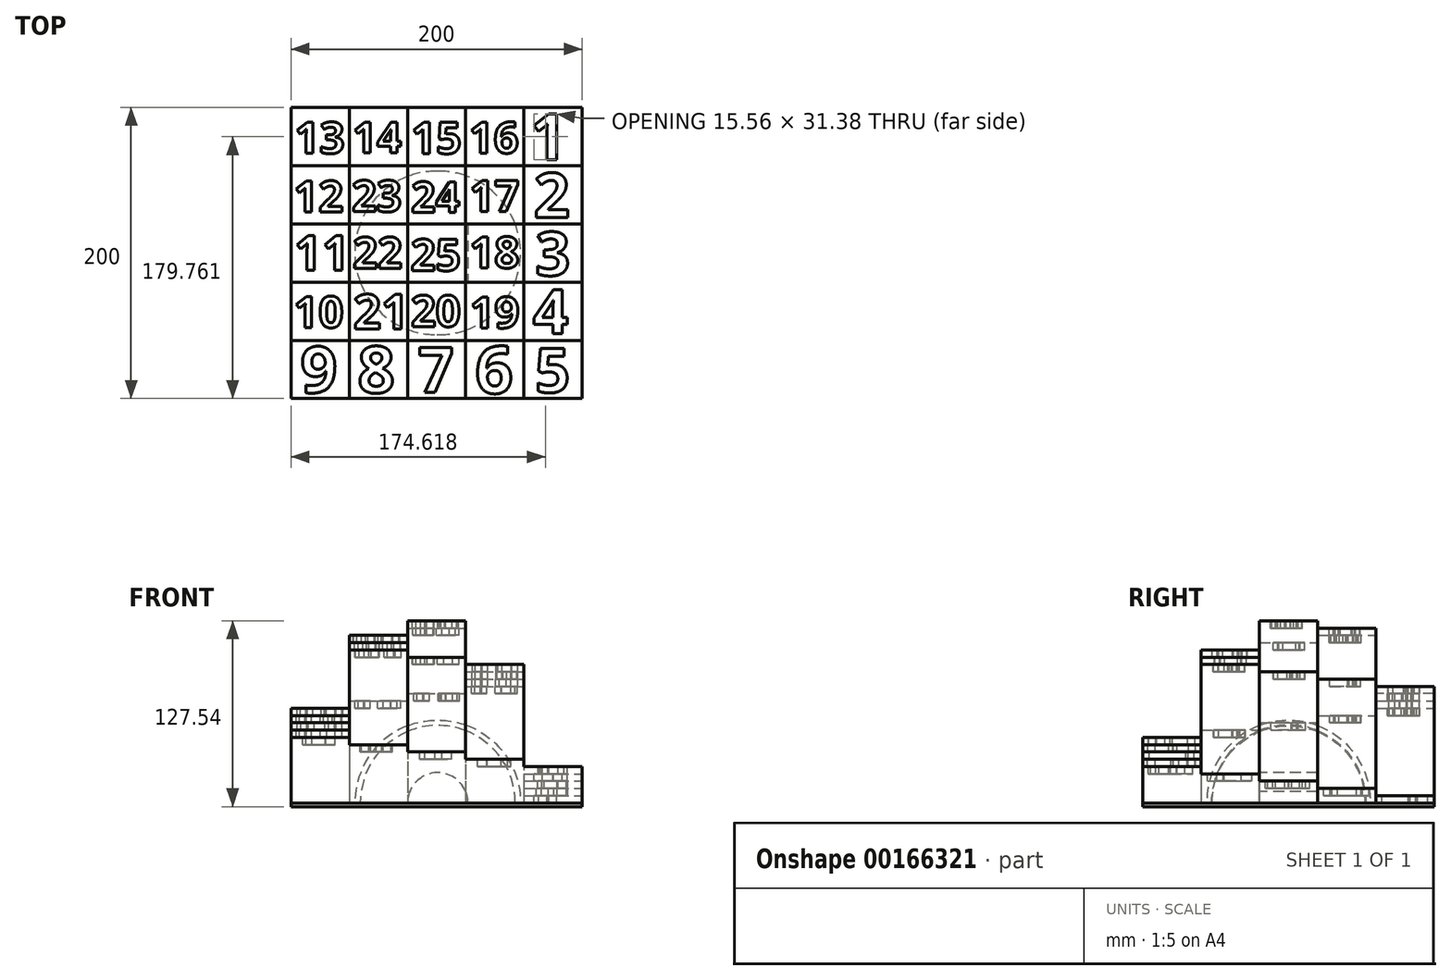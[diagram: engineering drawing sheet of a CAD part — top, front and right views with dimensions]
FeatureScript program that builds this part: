
annotation { "Feature Type Name" : "Feature", "Feature Type Description" : "" }
export const myFeature = defineFeature(function(context is Context, id is Id, definition is map)
    precondition{}
    {
        {
            var Q0;
            Q0=qCreatedBy(makeId("Top.planeOp"),FACE);
            var sketch = newSketch(context, id + "F0", { "sketchPlane" : qUnion([Q0])});
            skLineSegment(sketch, "E0.bottom", {"start": v(-166.14, 98.83) * mm, "end": v(33.86, 98.83) * mm});
            skLineSegment(sketch, "E0.top", {"start": v(-166.14, -101.17) * mm, "end": v(33.86, -101.17) * mm});
            skLineSegment(sketch, "E0.left", {"start": v(-166.14, 98.83) * mm, "end": v(-166.14, -101.17) * mm});
            skLineSegment(sketch, "E0.right", {"start": v(33.86, 98.83) * mm, "end": v(33.86, -101.17) * mm});
            skLineSegment(sketch, "E1", {"start": v(-166.14, 58.83) * mm, "end": v(33.86, 58.83) * mm});
            skLineSegment(sketch, "E2", {"start": v(-166.14, 18.83) * mm, "end": v(33.86, 18.83) * mm});
            skLineSegment(sketch, "E3", {"start": v(-166.14, -21.17) * mm, "end": v(33.86, -21.17) * mm});
            skLineSegment(sketch, "E4", {"start": v(-166.14, -61.17) * mm, "end": v(33.86, -61.17) * mm});
            skLineSegment(sketch, "E5", {"start": v(-126.14, 98.83) * mm, "end": v(-126.14, -101.17) * mm});
            skLineSegment(sketch, "E6", {"start": v(-86.14, 98.83) * mm, "end": v(-86.14, -101.17) * mm});
            skLineSegment(sketch, "E7", {"start": v(-46.14, 98.83) * mm, "end": v(-46.14, -101.17) * mm});
            skLineSegment(sketch, "E8", {"start": v(-6.14, 98.83) * mm, "end": v(-6.14, -101.17) * mm});
            skSolve(sketch);
        }
        {
            var Q0;
            {var subQ0=sQuery(id+"F0.wireOp",EDGE,"E0.left");var subQ1=sQuery(id+"F0.wireOp",EDGE,"E0.bottom");var subQ2=makeQuery(id+"F0.imprint","INTERSECT",VERTEX,{"derivedFrom":[subQ1,subQ0]});Q0=makeQuery(id+"F0.imprint","IMPRINT",FACE,{"disambiguationData":[TD([[makeQuery(id+"F0.imprint","IMPRINT",EDGE,{"disambiguationData":[TD([[subQ2,-1.0]])],"derivedFrom":subQ1}),-1.0]])]});}
            extrude(context, id + "F1", {"entities" : qUnion([Q0]), "depth" : 5 * mm});
        }
        {
            var Q0;
            Q0=makeQuery(id+"F1.opExtrude","CAP_FACE",FACE,{"disambiguationData":[OSD([sQuery(id+"F0.wireOp",EDGE,"E0.bottom"),sQuery(id+"F0.wireOp",EDGE,"E0.left"),sQuery(id+"F0.wireOp",EDGE,"E1"),sQuery(id+"F0.wireOp",EDGE,"E5")])],"isStart":true});
            var sketch = newSketch(context, id + "F2", { "sketchPlane" : qUnion([Q0])});
            skLineSegment(sketch, "E9.bottom", {"start": v(-166.14, -58.83) * mm, "end": v(-126.14, -58.83) * mm});
            skLineSegment(sketch, "E9.top", {"start": v(-166.14, -18.83) * mm, "end": v(-126.14, -18.83) * mm});
            skLineSegment(sketch, "E9.left", {"start": v(-166.14, -58.83) * mm, "end": v(-166.14, -18.83) * mm});
            skLineSegment(sketch, "E9.right", {"start": v(-126.14, -58.83) * mm, "end": v(-126.14, -18.83) * mm});
            skSolve(sketch);
        }
        {
            var Q0;
            Q0 = qSketchRegion(id + "F2", true);
            extrude(context, id + "F3", {"entities" : qUnion([Q0]), "oppositeDirection" : true, "depth" : 10 * mm});
        }
        {
            var Q0;
            Q0=makeQuery(id+"F3.opExtrude","CAP_FACE",FACE,{"disambiguationData":[OSD([sQuery(id+"F2.wireOp",EDGE,"E9.bottom"),sQuery(id+"F2.wireOp",EDGE,"E9.top"),sQuery(id+"F2.wireOp",EDGE,"E9.left"),sQuery(id+"F2.wireOp",EDGE,"E9.right")])],"isStart":true});
            var sketch = newSketch(context, id + "F4", { "sketchPlane" : qUnion([Q0])});
            skLineSegment(sketch, "E10.bottom", {"start": v(-166.14, -18.83) * mm, "end": v(-126.14, -18.83) * mm});
            skLineSegment(sketch, "E10.top", {"start": v(-166.14, 21.17) * mm, "end": v(-126.14, 21.17) * mm});
            skLineSegment(sketch, "E10.left", {"start": v(-166.14, -18.83) * mm, "end": v(-166.14, 21.17) * mm});
            skLineSegment(sketch, "E10.right", {"start": v(-126.14, -18.83) * mm, "end": v(-126.14, 21.17) * mm});
            skSolve(sketch);
        }
        {
            var Q0;
            Q0 = qSketchRegion(id + "F4", true);
            extrude(context, id + "F5", {"entities" : qUnion([Q0]), "oppositeDirection" : true, "depth" : 15 * mm});
        }
        {
            var Q0;
            Q0=makeQuery(id+"F5.opExtrude","CAP_FACE",FACE,{"disambiguationData":[OSD([sQuery(id+"F4.wireOp",EDGE,"E10.bottom"),sQuery(id+"F4.wireOp",EDGE,"E10.top"),sQuery(id+"F4.wireOp",EDGE,"E10.left"),sQuery(id+"F4.wireOp",EDGE,"E10.right")])],"isStart":true});
            var sketch = newSketch(context, id + "F6", { "sketchPlane" : qUnion([Q0])});
            skLineSegment(sketch, "E11.bottom", {"start": v(-166.14, 21.17) * mm, "end": v(-126.14, 21.17) * mm});
            skLineSegment(sketch, "E11.top", {"start": v(-166.14, 61.17) * mm, "end": v(-126.14, 61.17) * mm});
            skLineSegment(sketch, "E11.left", {"start": v(-166.14, 21.17) * mm, "end": v(-166.14, 61.17) * mm});
            skLineSegment(sketch, "E11.right", {"start": v(-126.14, 21.17) * mm, "end": v(-126.14, 61.17) * mm});
            skSolve(sketch);
        }
        {
            var Q0;
            Q0 = qSketchRegion(id + "F6", true);
            extrude(context, id + "F7", {"entities" : qUnion([Q0]), "operationType" : NewBodyOperationType.ADD, "oppositeDirection" : true, "depth" : 20 * mm});
        }
        {
            var Q0;
            Q0=makeQuery(id+"F7.boolean.opBoolean","MERGE",FACE,{"derivedFrom":[makeQuery(id+"F5.opExtrude","CAP_FACE",FACE,{"disambiguationData":[OSD([sQuery(id+"F4.wireOp",EDGE,"E10.bottom"),sQuery(id+"F4.wireOp",EDGE,"E10.top"),sQuery(id+"F4.wireOp",EDGE,"E10.left"),sQuery(id+"F4.wireOp",EDGE,"E10.right")])],"isStart":true}),makeQuery(id+"F7.opExtrude","CAP_FACE",FACE,{"disambiguationData":[OSD([sQuery(id+"F6.wireOp",EDGE,"E11.bottom"),sQuery(id+"F6.wireOp",EDGE,"E11.top"),sQuery(id+"F6.wireOp",EDGE,"E11.left"),sQuery(id+"F6.wireOp",EDGE,"E11.right")])],"isStart":true})]});
            var sketch = newSketch(context, id + "F8", { "sketchPlane" : qUnion([Q0])});
            skLineSegment(sketch, "E12.bottom", {"start": v(-166.14, 61.17) * mm, "end": v(-126.14, 61.17) * mm});
            skLineSegment(sketch, "E12.top", {"start": v(-166.14, 101.17) * mm, "end": v(-126.14, 101.17) * mm});
            skLineSegment(sketch, "E12.left", {"start": v(-166.14, 61.17) * mm, "end": v(-166.14, 101.17) * mm});
            skLineSegment(sketch, "E12.right", {"start": v(-126.14, 61.17) * mm, "end": v(-126.14, 101.17) * mm});
            skSolve(sketch);
        }
        {
            var Q0;
            Q0 = qSketchRegion(id + "F8", true);
            extrude(context, id + "F9", {"entities" : qUnion([Q0]), "oppositeDirection" : true, "depth" : 25 * mm});
        }
        {
            var Q0;
            Q0=makeQuery(id+"F9.opExtrude","CAP_FACE",FACE,{"disambiguationData":[OSD([sQuery(id+"F8.wireOp",EDGE,"E12.bottom"),sQuery(id+"F8.wireOp",EDGE,"E12.top"),sQuery(id+"F8.wireOp",EDGE,"E12.left"),sQuery(id+"F8.wireOp",EDGE,"E12.right")])],"isStart":true});
            var sketch = newSketch(context, id + "F10", { "sketchPlane" : qUnion([Q0])});
            skLineSegment(sketch, "E13.bottom", {"start": v(-166.14, 61.17) * mm, "end": v(-206.14, 61.17) * mm});
            skLineSegment(sketch, "E13.top", {"start": v(-166.14, 101.17) * mm, "end": v(-206.14, 101.17) * mm});
            skLineSegment(sketch, "E13.left", {"start": v(-166.14, 61.17) * mm, "end": v(-166.14, 101.17) * mm});
            skLineSegment(sketch, "E13.right", {"start": v(-206.14, 61.17) * mm, "end": v(-206.14, 101.17) * mm});
            skSolve(sketch);
        }
        {
            var Q0;
            Q0 = qSketchRegion(id + "F10", true);
            extrude(context, id + "F11", {"entities" : qUnion([Q0]), "operationType" : NewBodyOperationType.ADD, "oppositeDirection" : true, "depth" : 30 * mm});
        }
        {
            var Q0;
            Q0=makeQuery(id+"F11.boolean.opBoolean","MERGE",FACE,{"derivedFrom":[makeQuery(id+"F9.opExtrude","CAP_FACE",FACE,{"disambiguationData":[OSD([sQuery(id+"F8.wireOp",EDGE,"E12.bottom"),sQuery(id+"F8.wireOp",EDGE,"E12.top"),sQuery(id+"F8.wireOp",EDGE,"E12.left"),sQuery(id+"F8.wireOp",EDGE,"E12.right")])],"isStart":true}),makeQuery(id+"F11.opExtrude","CAP_FACE",FACE,{"disambiguationData":[OSD([sQuery(id+"F10.wireOp",EDGE,"E13.bottom"),sQuery(id+"F10.wireOp",EDGE,"E13.top"),sQuery(id+"F10.wireOp",EDGE,"E13.left"),sQuery(id+"F10.wireOp",EDGE,"E13.right")])],"isStart":true})]});
            var sketch = newSketch(context, id + "F12", { "sketchPlane" : qUnion([Q0])});
            skLineSegment(sketch, "E14.bottom", {"start": v(-206.14, 61.17) * mm, "end": v(-246.14, 61.17) * mm});
            skLineSegment(sketch, "E14.top", {"start": v(-206.14, 101.17) * mm, "end": v(-246.14, 101.17) * mm});
            skLineSegment(sketch, "E14.left", {"start": v(-206.14, 61.17) * mm, "end": v(-206.14, 101.17) * mm});
            skLineSegment(sketch, "E14.right", {"start": v(-246.14, 61.17) * mm, "end": v(-246.14, 101.17) * mm});
            skSolve(sketch);
        }
        {
            var Q0;
            Q0 = qSketchRegion(id + "F12", true);
            extrude(context, id + "F13", {"entities" : qUnion([Q0]), "operationType" : NewBodyOperationType.ADD, "oppositeDirection" : true, "depth" : 35 * mm});
        }
        {
            var Q0;
            Q0=makeQuery(id+"F13.boolean.opBoolean","MERGE",FACE,{"derivedFrom":[makeQuery(id+"F11.boolean.opBoolean","MERGE",FACE,{"derivedFrom":[makeQuery(id+"F9.opExtrude","CAP_FACE",FACE,{"disambiguationData":[OSD([sQuery(id+"F8.wireOp",EDGE,"E12.bottom"),sQuery(id+"F8.wireOp",EDGE,"E12.top"),sQuery(id+"F8.wireOp",EDGE,"E12.left"),sQuery(id+"F8.wireOp",EDGE,"E12.right")])],"isStart":true}),makeQuery(id+"F11.opExtrude","CAP_FACE",FACE,{"disambiguationData":[OSD([sQuery(id+"F10.wireOp",EDGE,"E13.bottom"),sQuery(id+"F10.wireOp",EDGE,"E13.top"),sQuery(id+"F10.wireOp",EDGE,"E13.left"),sQuery(id+"F10.wireOp",EDGE,"E13.right")])],"isStart":true})]}),makeQuery(id+"F13.opExtrude","CAP_FACE",FACE,{"disambiguationData":[OSD([sQuery(id+"F12.wireOp",EDGE,"E14.bottom"),sQuery(id+"F12.wireOp",EDGE,"E14.top"),sQuery(id+"F12.wireOp",EDGE,"E14.left"),sQuery(id+"F12.wireOp",EDGE,"E14.right")])],"isStart":true})]});
            var sketch = newSketch(context, id + "F14", { "sketchPlane" : qUnion([Q0])});
            skLineSegment(sketch, "E15.bottom", {"start": v(-246.14, 61.17) * mm, "end": v(-286.14, 61.17) * mm});
            skLineSegment(sketch, "E15.top", {"start": v(-246.14, 101.17) * mm, "end": v(-286.14, 101.17) * mm});
            skLineSegment(sketch, "E15.left", {"start": v(-246.14, 61.17) * mm, "end": v(-246.14, 101.17) * mm});
            skLineSegment(sketch, "E15.right", {"start": v(-286.14, 61.17) * mm, "end": v(-286.14, 101.17) * mm});
            skSolve(sketch);
        }
        {
            var Q0;
            Q0 = qSketchRegion(id + "F14", true);
            extrude(context, id + "F15", {"entities" : qUnion([Q0]), "operationType" : NewBodyOperationType.ADD, "oppositeDirection" : true, "depth" : 40 * mm});
        }
        {
            var Q0;
            Q0=makeQuery(id+"F15.boolean.opBoolean","MERGE",FACE,{"derivedFrom":[makeQuery(id+"F13.boolean.opBoolean","MERGE",FACE,{"derivedFrom":[makeQuery(id+"F11.boolean.opBoolean","MERGE",FACE,{"derivedFrom":[makeQuery(id+"F9.opExtrude","CAP_FACE",FACE,{"disambiguationData":[OSD([sQuery(id+"F8.wireOp",EDGE,"E12.bottom"),sQuery(id+"F8.wireOp",EDGE,"E12.top"),sQuery(id+"F8.wireOp",EDGE,"E12.left"),sQuery(id+"F8.wireOp",EDGE,"E12.right")])],"isStart":true}),makeQuery(id+"F11.opExtrude","CAP_FACE",FACE,{"disambiguationData":[OSD([sQuery(id+"F10.wireOp",EDGE,"E13.bottom"),sQuery(id+"F10.wireOp",EDGE,"E13.top"),sQuery(id+"F10.wireOp",EDGE,"E13.left"),sQuery(id+"F10.wireOp",EDGE,"E13.right")])],"isStart":true})]}),makeQuery(id+"F13.opExtrude","CAP_FACE",FACE,{"disambiguationData":[OSD([sQuery(id+"F12.wireOp",EDGE,"E14.bottom"),sQuery(id+"F12.wireOp",EDGE,"E14.top"),sQuery(id+"F12.wireOp",EDGE,"E14.left"),sQuery(id+"F12.wireOp",EDGE,"E14.right")])],"isStart":true})]}),makeQuery(id+"F15.opExtrude","CAP_FACE",FACE,{"disambiguationData":[OSD([sQuery(id+"F14.wireOp",EDGE,"E15.bottom"),sQuery(id+"F14.wireOp",EDGE,"E15.top"),sQuery(id+"F14.wireOp",EDGE,"E15.left"),sQuery(id+"F14.wireOp",EDGE,"E15.right")])],"isStart":true})]});
            var sketch = newSketch(context, id + "F16", { "sketchPlane" : qUnion([Q0])});
            skLineSegment(sketch, "E16.bottom", {"start": v(-286.14, 61.17) * mm, "end": v(-326.14, 61.17) * mm});
            skLineSegment(sketch, "E16.top", {"start": v(-286.14, 101.17) * mm, "end": v(-326.14, 101.17) * mm});
            skLineSegment(sketch, "E16.left", {"start": v(-286.14, 61.17) * mm, "end": v(-286.14, 101.17) * mm});
            skLineSegment(sketch, "E16.right", {"start": v(-326.14, 61.17) * mm, "end": v(-326.14, 101.17) * mm});
            skSolve(sketch);
        }
        {
            var Q0;
            Q0 = qSketchRegion(id + "F16", true);
            extrude(context, id + "F17", {"entities" : qUnion([Q0]), "operationType" : NewBodyOperationType.ADD, "oppositeDirection" : true, "depth" : 45 * mm});
        }
        {
            var Q0;
            Q0=makeQuery(id+"F17.boolean.opBoolean","MERGE",FACE,{"derivedFrom":[makeQuery(id+"F15.boolean.opBoolean","MERGE",FACE,{"derivedFrom":[makeQuery(id+"F13.boolean.opBoolean","MERGE",FACE,{"derivedFrom":[makeQuery(id+"F11.boolean.opBoolean","MERGE",FACE,{"derivedFrom":[makeQuery(id+"F9.opExtrude","CAP_FACE",FACE,{"disambiguationData":[OSD([sQuery(id+"F8.wireOp",EDGE,"E12.bottom"),sQuery(id+"F8.wireOp",EDGE,"E12.top"),sQuery(id+"F8.wireOp",EDGE,"E12.left"),sQuery(id+"F8.wireOp",EDGE,"E12.right")])],"isStart":true}),makeQuery(id+"F11.opExtrude","CAP_FACE",FACE,{"disambiguationData":[OSD([sQuery(id+"F10.wireOp",EDGE,"E13.bottom"),sQuery(id+"F10.wireOp",EDGE,"E13.top"),sQuery(id+"F10.wireOp",EDGE,"E13.left"),sQuery(id+"F10.wireOp",EDGE,"E13.right")])],"isStart":true})]}),makeQuery(id+"F13.opExtrude","CAP_FACE",FACE,{"disambiguationData":[OSD([sQuery(id+"F12.wireOp",EDGE,"E14.bottom"),sQuery(id+"F12.wireOp",EDGE,"E14.top"),sQuery(id+"F12.wireOp",EDGE,"E14.left"),sQuery(id+"F12.wireOp",EDGE,"E14.right")])],"isStart":true})]}),makeQuery(id+"F15.opExtrude","CAP_FACE",FACE,{"disambiguationData":[OSD([sQuery(id+"F14.wireOp",EDGE,"E15.bottom"),sQuery(id+"F14.wireOp",EDGE,"E15.top"),sQuery(id+"F14.wireOp",EDGE,"E15.left"),sQuery(id+"F14.wireOp",EDGE,"E15.right")])],"isStart":true})]}),makeQuery(id+"F17.opExtrude","CAP_FACE",FACE,{"disambiguationData":[OSD([sQuery(id+"F16.wireOp",EDGE,"E16.bottom"),sQuery(id+"F16.wireOp",EDGE,"E16.top"),sQuery(id+"F16.wireOp",EDGE,"E16.left"),sQuery(id+"F16.wireOp",EDGE,"E16.right")])],"isStart":true})]});
            var sketch = newSketch(context, id + "F18", { "sketchPlane" : qUnion([Q0])});
            skLineSegment(sketch, "E17.bottom", {"start": v(-326.14, 61.17) * mm, "end": v(-286.14, 61.17) * mm});
            skLineSegment(sketch, "E17.top", {"start": v(-326.14, 21.17) * mm, "end": v(-286.14, 21.17) * mm});
            skLineSegment(sketch, "E17.left", {"start": v(-326.14, 61.17) * mm, "end": v(-326.14, 21.17) * mm});
            skLineSegment(sketch, "E17.right", {"start": v(-286.14, 61.17) * mm, "end": v(-286.14, 21.17) * mm});
            skSolve(sketch);
        }
        {
            var Q0;
            Q0 = qSketchRegion(id + "F18", true);
            extrude(context, id + "F19", {"entities" : qUnion([Q0]), "operationType" : NewBodyOperationType.ADD, "oppositeDirection" : true, "depth" : 50 * mm});
        }
        {
            var Q0;
            Q0=makeQuery(id+"F19.boolean.opBoolean","MERGE",FACE,{"derivedFrom":[makeQuery(id+"F17.boolean.opBoolean","MERGE",FACE,{"derivedFrom":[makeQuery(id+"F15.boolean.opBoolean","MERGE",FACE,{"derivedFrom":[makeQuery(id+"F13.boolean.opBoolean","MERGE",FACE,{"derivedFrom":[makeQuery(id+"F11.boolean.opBoolean","MERGE",FACE,{"derivedFrom":[makeQuery(id+"F9.opExtrude","CAP_FACE",FACE,{"disambiguationData":[OSD([sQuery(id+"F8.wireOp",EDGE,"E12.bottom"),sQuery(id+"F8.wireOp",EDGE,"E12.top"),sQuery(id+"F8.wireOp",EDGE,"E12.left"),sQuery(id+"F8.wireOp",EDGE,"E12.right")])],"isStart":true}),makeQuery(id+"F11.opExtrude","CAP_FACE",FACE,{"disambiguationData":[OSD([sQuery(id+"F10.wireOp",EDGE,"E13.bottom"),sQuery(id+"F10.wireOp",EDGE,"E13.top"),sQuery(id+"F10.wireOp",EDGE,"E13.left"),sQuery(id+"F10.wireOp",EDGE,"E13.right")])],"isStart":true})]}),makeQuery(id+"F13.opExtrude","CAP_FACE",FACE,{"disambiguationData":[OSD([sQuery(id+"F12.wireOp",EDGE,"E14.bottom"),sQuery(id+"F12.wireOp",EDGE,"E14.top"),sQuery(id+"F12.wireOp",EDGE,"E14.left"),sQuery(id+"F12.wireOp",EDGE,"E14.right")])],"isStart":true})]}),makeQuery(id+"F15.opExtrude","CAP_FACE",FACE,{"disambiguationData":[OSD([sQuery(id+"F14.wireOp",EDGE,"E15.bottom"),sQuery(id+"F14.wireOp",EDGE,"E15.top"),sQuery(id+"F14.wireOp",EDGE,"E15.left"),sQuery(id+"F14.wireOp",EDGE,"E15.right")])],"isStart":true})]}),makeQuery(id+"F17.opExtrude","CAP_FACE",FACE,{"disambiguationData":[OSD([sQuery(id+"F16.wireOp",EDGE,"E16.bottom"),sQuery(id+"F16.wireOp",EDGE,"E16.top"),sQuery(id+"F16.wireOp",EDGE,"E16.left"),sQuery(id+"F16.wireOp",EDGE,"E16.right")])],"isStart":true})]}),makeQuery(id+"F19.opExtrude","CAP_FACE",FACE,{"disambiguationData":[OSD([sQuery(id+"F18.wireOp",EDGE,"E17.bottom"),sQuery(id+"F18.wireOp",EDGE,"E17.top"),sQuery(id+"F18.wireOp",EDGE,"E17.left"),sQuery(id+"F18.wireOp",EDGE,"E17.right")])],"isStart":true})]});
            var sketch = newSketch(context, id + "F20", { "sketchPlane" : qUnion([Q0])});
            skLineSegment(sketch, "E18.bottom", {"start": v(-326.14, 21.17) * mm, "end": v(-286.14, 21.17) * mm});
            skLineSegment(sketch, "E18.top", {"start": v(-326.14, -18.83) * mm, "end": v(-286.14, -18.83) * mm});
            skLineSegment(sketch, "E18.left", {"start": v(-326.14, 21.17) * mm, "end": v(-326.14, -18.83) * mm});
            skLineSegment(sketch, "E18.right", {"start": v(-286.14, 21.17) * mm, "end": v(-286.14, -18.83) * mm});
            skSolve(sketch);
        }
        {
            var Q0;
            Q0 = qSketchRegion(id + "F20", true);
            extrude(context, id + "F21", {"entities" : qUnion([Q0]), "operationType" : NewBodyOperationType.ADD, "oppositeDirection" : true, "depth" : 55 * mm});
        }
        {
            var Q0;
            Q0=makeQuery(id+"F21.boolean.opBoolean","MERGE",FACE,{"derivedFrom":[makeQuery(id+"F19.boolean.opBoolean","MERGE",FACE,{"derivedFrom":[makeQuery(id+"F17.boolean.opBoolean","MERGE",FACE,{"derivedFrom":[makeQuery(id+"F15.boolean.opBoolean","MERGE",FACE,{"derivedFrom":[makeQuery(id+"F13.boolean.opBoolean","MERGE",FACE,{"derivedFrom":[makeQuery(id+"F11.boolean.opBoolean","MERGE",FACE,{"derivedFrom":[makeQuery(id+"F9.opExtrude","CAP_FACE",FACE,{"disambiguationData":[OSD([sQuery(id+"F8.wireOp",EDGE,"E12.bottom"),sQuery(id+"F8.wireOp",EDGE,"E12.top"),sQuery(id+"F8.wireOp",EDGE,"E12.left"),sQuery(id+"F8.wireOp",EDGE,"E12.right")])],"isStart":true}),makeQuery(id+"F11.opExtrude","CAP_FACE",FACE,{"disambiguationData":[OSD([sQuery(id+"F10.wireOp",EDGE,"E13.bottom"),sQuery(id+"F10.wireOp",EDGE,"E13.top"),sQuery(id+"F10.wireOp",EDGE,"E13.left"),sQuery(id+"F10.wireOp",EDGE,"E13.right")])],"isStart":true})]}),makeQuery(id+"F13.opExtrude","CAP_FACE",FACE,{"disambiguationData":[OSD([sQuery(id+"F12.wireOp",EDGE,"E14.bottom"),sQuery(id+"F12.wireOp",EDGE,"E14.top"),sQuery(id+"F12.wireOp",EDGE,"E14.left"),sQuery(id+"F12.wireOp",EDGE,"E14.right")])],"isStart":true})]}),makeQuery(id+"F15.opExtrude","CAP_FACE",FACE,{"disambiguationData":[OSD([sQuery(id+"F14.wireOp",EDGE,"E15.bottom"),sQuery(id+"F14.wireOp",EDGE,"E15.top"),sQuery(id+"F14.wireOp",EDGE,"E15.left"),sQuery(id+"F14.wireOp",EDGE,"E15.right")])],"isStart":true})]}),makeQuery(id+"F17.opExtrude","CAP_FACE",FACE,{"disambiguationData":[OSD([sQuery(id+"F16.wireOp",EDGE,"E16.bottom"),sQuery(id+"F16.wireOp",EDGE,"E16.top"),sQuery(id+"F16.wireOp",EDGE,"E16.left"),sQuery(id+"F16.wireOp",EDGE,"E16.right")])],"isStart":true})]}),makeQuery(id+"F19.opExtrude","CAP_FACE",FACE,{"disambiguationData":[OSD([sQuery(id+"F18.wireOp",EDGE,"E17.bottom"),sQuery(id+"F18.wireOp",EDGE,"E17.top"),sQuery(id+"F18.wireOp",EDGE,"E17.left"),sQuery(id+"F18.wireOp",EDGE,"E17.right")])],"isStart":true})]}),makeQuery(id+"F21.opExtrude","CAP_FACE",FACE,{"disambiguationData":[OSD([sQuery(id+"F20.wireOp",EDGE,"E18.bottom"),sQuery(id+"F20.wireOp",EDGE,"E18.top"),sQuery(id+"F20.wireOp",EDGE,"E18.left"),sQuery(id+"F20.wireOp",EDGE,"E18.right")])],"isStart":true})]});
            var sketch = newSketch(context, id + "F22", { "sketchPlane" : qUnion([Q0])});
            skLineSegment(sketch, "E19.bottom", {"start": v(-326.14, -18.83) * mm, "end": v(-286.14, -18.83) * mm});
            skLineSegment(sketch, "E19.top", {"start": v(-326.14, -58.83) * mm, "end": v(-286.14, -58.83) * mm});
            skLineSegment(sketch, "E19.left", {"start": v(-326.14, -18.83) * mm, "end": v(-326.14, -58.83) * mm});
            skLineSegment(sketch, "E19.right", {"start": v(-286.14, -18.83) * mm, "end": v(-286.14, -58.83) * mm});
            skSolve(sketch);
        }
        {
            var Q0;
            Q0 = qSketchRegion(id + "F22", true);
            extrude(context, id + "F23", {"entities" : qUnion([Q0]), "operationType" : NewBodyOperationType.ADD, "oppositeDirection" : true, "depth" : 60 * mm});
        }
        {
            var Q0;
            Q0=makeQuery(id+"F23.boolean.opBoolean","MERGE",FACE,{"derivedFrom":[makeQuery(id+"F21.boolean.opBoolean","MERGE",FACE,{"derivedFrom":[makeQuery(id+"F19.boolean.opBoolean","MERGE",FACE,{"derivedFrom":[makeQuery(id+"F17.boolean.opBoolean","MERGE",FACE,{"derivedFrom":[makeQuery(id+"F15.boolean.opBoolean","MERGE",FACE,{"derivedFrom":[makeQuery(id+"F13.boolean.opBoolean","MERGE",FACE,{"derivedFrom":[makeQuery(id+"F11.boolean.opBoolean","MERGE",FACE,{"derivedFrom":[makeQuery(id+"F9.opExtrude","CAP_FACE",FACE,{"disambiguationData":[OSD([sQuery(id+"F8.wireOp",EDGE,"E12.bottom"),sQuery(id+"F8.wireOp",EDGE,"E12.top"),sQuery(id+"F8.wireOp",EDGE,"E12.left"),sQuery(id+"F8.wireOp",EDGE,"E12.right")])],"isStart":true}),makeQuery(id+"F11.opExtrude","CAP_FACE",FACE,{"disambiguationData":[OSD([sQuery(id+"F10.wireOp",EDGE,"E13.bottom"),sQuery(id+"F10.wireOp",EDGE,"E13.top"),sQuery(id+"F10.wireOp",EDGE,"E13.left"),sQuery(id+"F10.wireOp",EDGE,"E13.right")])],"isStart":true})]}),makeQuery(id+"F13.opExtrude","CAP_FACE",FACE,{"disambiguationData":[OSD([sQuery(id+"F12.wireOp",EDGE,"E14.bottom"),sQuery(id+"F12.wireOp",EDGE,"E14.top"),sQuery(id+"F12.wireOp",EDGE,"E14.left"),sQuery(id+"F12.wireOp",EDGE,"E14.right")])],"isStart":true})]}),makeQuery(id+"F15.opExtrude","CAP_FACE",FACE,{"disambiguationData":[OSD([sQuery(id+"F14.wireOp",EDGE,"E15.bottom"),sQuery(id+"F14.wireOp",EDGE,"E15.top"),sQuery(id+"F14.wireOp",EDGE,"E15.left"),sQuery(id+"F14.wireOp",EDGE,"E15.right")])],"isStart":true})]}),makeQuery(id+"F17.opExtrude","CAP_FACE",FACE,{"disambiguationData":[OSD([sQuery(id+"F16.wireOp",EDGE,"E16.bottom"),sQuery(id+"F16.wireOp",EDGE,"E16.top"),sQuery(id+"F16.wireOp",EDGE,"E16.left"),sQuery(id+"F16.wireOp",EDGE,"E16.right")])],"isStart":true})]}),makeQuery(id+"F19.opExtrude","CAP_FACE",FACE,{"disambiguationData":[OSD([sQuery(id+"F18.wireOp",EDGE,"E17.bottom"),sQuery(id+"F18.wireOp",EDGE,"E17.top"),sQuery(id+"F18.wireOp",EDGE,"E17.left"),sQuery(id+"F18.wireOp",EDGE,"E17.right")])],"isStart":true})]}),makeQuery(id+"F21.opExtrude","CAP_FACE",FACE,{"disambiguationData":[OSD([sQuery(id+"F20.wireOp",EDGE,"E18.bottom"),sQuery(id+"F20.wireOp",EDGE,"E18.top"),sQuery(id+"F20.wireOp",EDGE,"E18.left"),sQuery(id+"F20.wireOp",EDGE,"E18.right")])],"isStart":true})]}),makeQuery(id+"F23.opExtrude","CAP_FACE",FACE,{"disambiguationData":[OSD([sQuery(id+"F22.wireOp",EDGE,"E19.bottom"),sQuery(id+"F22.wireOp",EDGE,"E19.top"),sQuery(id+"F22.wireOp",EDGE,"E19.left"),sQuery(id+"F22.wireOp",EDGE,"E19.right")])],"isStart":true})]});
            var sketch = newSketch(context, id + "F24", { "sketchPlane" : qUnion([Q0])});
            skLineSegment(sketch, "E20.bottom", {"start": v(-326.14, -58.83) * mm, "end": v(-286.14, -58.83) * mm});
            skLineSegment(sketch, "E20.top", {"start": v(-326.14, -98.83) * mm, "end": v(-286.14, -98.83) * mm});
            skLineSegment(sketch, "E20.left", {"start": v(-326.14, -58.83) * mm, "end": v(-326.14, -98.83) * mm});
            skLineSegment(sketch, "E20.right", {"start": v(-286.14, -58.83) * mm, "end": v(-286.14, -98.83) * mm});
            skSolve(sketch);
        }
        {
            var Q0;
            Q0 = qSketchRegion(id + "F24", true);
            extrude(context, id + "F25", {"entities" : qUnion([Q0]), "oppositeDirection" : true, "depth" : 65 * mm});
        }
        {
            var Q0;
            Q0=makeQuery(id+"F25.opExtrude","CAP_FACE",FACE,{"disambiguationData":[OSD([sQuery(id+"F24.wireOp",EDGE,"E20.bottom"),sQuery(id+"F24.wireOp",EDGE,"E20.top"),sQuery(id+"F24.wireOp",EDGE,"E20.left"),sQuery(id+"F24.wireOp",EDGE,"E20.right")])],"isStart":true});
            var sketch = newSketch(context, id + "F26", { "sketchPlane" : qUnion([Q0])});
            skLineSegment(sketch, "E21.bottom", {"start": v(-286.14, -98.83) * mm, "end": v(-246.14, -98.83) * mm});
            skLineSegment(sketch, "E21.top", {"start": v(-286.14, -58.83) * mm, "end": v(-246.14, -58.83) * mm});
            skLineSegment(sketch, "E21.left", {"start": v(-286.14, -98.83) * mm, "end": v(-286.14, -58.83) * mm});
            skLineSegment(sketch, "E21.right", {"start": v(-246.14, -98.83) * mm, "end": v(-246.14, -58.83) * mm});
            skSolve(sketch);
        }
        {
            var Q0;
            Q0 = qSketchRegion(id + "F26", true);
            extrude(context, id + "F27", {"entities" : qUnion([Q0]), "operationType" : NewBodyOperationType.ADD, "oppositeDirection" : true, "depth" : 70 * mm});
        }
        {
            var Q0;
            Q0=makeQuery(id+"F27.boolean.opBoolean","MERGE",FACE,{"derivedFrom":[makeQuery(id+"F25.opExtrude","CAP_FACE",FACE,{"disambiguationData":[OSD([sQuery(id+"F24.wireOp",EDGE,"E20.bottom"),sQuery(id+"F24.wireOp",EDGE,"E20.top"),sQuery(id+"F24.wireOp",EDGE,"E20.left"),sQuery(id+"F24.wireOp",EDGE,"E20.right")])],"isStart":true}),makeQuery(id+"F27.opExtrude","CAP_FACE",FACE,{"disambiguationData":[OSD([sQuery(id+"F26.wireOp",EDGE,"E21.bottom"),sQuery(id+"F26.wireOp",EDGE,"E21.top"),sQuery(id+"F26.wireOp",EDGE,"E21.left"),sQuery(id+"F26.wireOp",EDGE,"E21.right")])],"isStart":true})]});
            var sketch = newSketch(context, id + "F28", { "sketchPlane" : qUnion([Q0])});
            skLineSegment(sketch, "E22.bottom", {"start": v(-246.14, -98.83) * mm, "end": v(-206.14, -98.83) * mm});
            skLineSegment(sketch, "E22.top", {"start": v(-246.14, -58.83) * mm, "end": v(-206.14, -58.83) * mm});
            skLineSegment(sketch, "E22.left", {"start": v(-246.14, -98.83) * mm, "end": v(-246.14, -58.83) * mm});
            skLineSegment(sketch, "E22.right", {"start": v(-206.14, -98.83) * mm, "end": v(-206.14, -58.83) * mm});
            skSolve(sketch);
        }
        {
            var Q0;
            Q0 = qSketchRegion(id + "F28", true);
            extrude(context, id + "F29", {"entities" : qUnion([Q0]), "oppositeDirection" : true, "depth" : 75 * mm});
        }
        {
            var Q0;
            Q0=makeQuery(id+"F29.opExtrude","CAP_FACE",FACE,{"disambiguationData":[OSD([sQuery(id+"F28.wireOp",EDGE,"E22.bottom"),sQuery(id+"F28.wireOp",EDGE,"E22.top"),sQuery(id+"F28.wireOp",EDGE,"E22.left"),sQuery(id+"F28.wireOp",EDGE,"E22.right")])],"isStart":true});
            var sketch = newSketch(context, id + "F30", { "sketchPlane" : qUnion([Q0])});
            skLineSegment(sketch, "E23.bottom", {"start": v(-206.14, -98.83) * mm, "end": v(-166.14, -98.83) * mm});
            skLineSegment(sketch, "E23.top", {"start": v(-206.14, -58.83) * mm, "end": v(-166.14, -58.83) * mm});
            skLineSegment(sketch, "E23.left", {"start": v(-206.14, -98.83) * mm, "end": v(-206.14, -58.83) * mm});
            skLineSegment(sketch, "E23.right", {"start": v(-166.14, -98.83) * mm, "end": v(-166.14, -58.83) * mm});
            skSolve(sketch);
        }
        {
            var Q0;
            Q0 = qSketchRegion(id + "F30", true);
            extrude(context, id + "F31", {"entities" : qUnion([Q0]), "oppositeDirection" : true, "depth" : 80 * mm});
        }
        {
            var Q0;
            Q0=makeQuery(id+"F31.opExtrude","CAP_FACE",FACE,{"disambiguationData":[OSD([sQuery(id+"F30.wireOp",EDGE,"E23.bottom"),sQuery(id+"F30.wireOp",EDGE,"E23.top"),sQuery(id+"F30.wireOp",EDGE,"E23.left"),sQuery(id+"F30.wireOp",EDGE,"E23.right")])],"isStart":true});
            var sketch = newSketch(context, id + "F32", { "sketchPlane" : qUnion([Q0])});
            skLineSegment(sketch, "E24.bottom", {"start": v(-166.14, -58.83) * mm, "end": v(-206.14, -58.83) * mm});
            skLineSegment(sketch, "E24.top", {"start": v(-166.14, -18.83) * mm, "end": v(-206.14, -18.83) * mm});
            skLineSegment(sketch, "E24.left", {"start": v(-166.14, -58.83) * mm, "end": v(-166.14, -18.83) * mm});
            skLineSegment(sketch, "E24.right", {"start": v(-206.14, -58.83) * mm, "end": v(-206.14, -18.83) * mm});
            skSolve(sketch);
        }
        {
            var Q0;
            Q0 = qSketchRegion(id + "F32", true);
            extrude(context, id + "F33", {"entities" : qUnion([Q0]), "oppositeDirection" : true, "depth" : 85 * mm});
        }
        {
            var Q0;
            Q0=makeQuery(id+"F33.opExtrude","CAP_FACE",FACE,{"disambiguationData":[OSD([sQuery(id+"F32.wireOp",EDGE,"E24.bottom"),sQuery(id+"F32.wireOp",EDGE,"E24.top"),sQuery(id+"F32.wireOp",EDGE,"E24.left"),sQuery(id+"F32.wireOp",EDGE,"E24.right")])],"isStart":true});
            var sketch = newSketch(context, id + "F34", { "sketchPlane" : qUnion([Q0])});
            skLineSegment(sketch, "E25.bottom", {"start": v(-206.14, -18.83) * mm, "end": v(-166.14, -18.83) * mm});
            skLineSegment(sketch, "E25.top", {"start": v(-206.14, 21.17) * mm, "end": v(-166.14, 21.17) * mm});
            skLineSegment(sketch, "E25.left", {"start": v(-206.14, -18.83) * mm, "end": v(-206.14, 21.17) * mm});
            skLineSegment(sketch, "E25.right", {"start": v(-166.14, -18.83) * mm, "end": v(-166.14, 21.17) * mm});
            skSolve(sketch);
        }
        {
            var Q0;
            Q0 = qSketchRegion(id + "F34", true);
            extrude(context, id + "F35", {"entities" : qUnion([Q0]), "oppositeDirection" : true, "depth" : 90 * mm});
        }
        {
            var Q0;
            Q0=makeQuery(id+"F35.opExtrude","CAP_FACE",FACE,{"disambiguationData":[OSD([sQuery(id+"F34.wireOp",EDGE,"E25.bottom"),sQuery(id+"F34.wireOp",EDGE,"E25.top"),sQuery(id+"F34.wireOp",EDGE,"E25.left"),sQuery(id+"F34.wireOp",EDGE,"E25.right")])],"isStart":true});
            var sketch = newSketch(context, id + "F36", { "sketchPlane" : qUnion([Q0])});
            skLineSegment(sketch, "E26.bottom", {"start": v(-206.14, 21.17) * mm, "end": v(-166.14, 21.17) * mm});
            skLineSegment(sketch, "E26.top", {"start": v(-206.14, 61.17) * mm, "end": v(-166.14, 61.17) * mm});
            skLineSegment(sketch, "E26.left", {"start": v(-206.14, 21.17) * mm, "end": v(-206.14, 61.17) * mm});
            skLineSegment(sketch, "E26.right", {"start": v(-166.14, 21.17) * mm, "end": v(-166.14, 61.17) * mm});
            skSolve(sketch);
        }
        {
            var Q0;
            Q0 = qSketchRegion(id + "F36", true);
            extrude(context, id + "F37", {"entities" : qUnion([Q0]), "oppositeDirection" : true, "depth" : 95 * mm});
        }
        {
            var Q0;
            Q0=makeQuery(id+"F37.opExtrude","CAP_FACE",FACE,{"disambiguationData":[OSD([sQuery(id+"F36.wireOp",EDGE,"E26.bottom"),sQuery(id+"F36.wireOp",EDGE,"E26.top"),sQuery(id+"F36.wireOp",EDGE,"E26.left"),sQuery(id+"F36.wireOp",EDGE,"E26.right")])],"isStart":true});
            var sketch = newSketch(context, id + "F38", { "sketchPlane" : qUnion([Q0])});
            skLineSegment(sketch, "E27.bottom", {"start": v(-206.14, 61.17) * mm, "end": v(-246.14, 61.17) * mm});
            skLineSegment(sketch, "E27.top", {"start": v(-206.14, 21.17) * mm, "end": v(-246.14, 21.17) * mm});
            skLineSegment(sketch, "E27.left", {"start": v(-206.14, 61.17) * mm, "end": v(-206.14, 21.17) * mm});
            skLineSegment(sketch, "E27.right", {"start": v(-246.14, 61.17) * mm, "end": v(-246.14, 21.17) * mm});
            skSolve(sketch);
        }
        {
            var Q0;
            Q0 = qSketchRegion(id + "F38", true);
            extrude(context, id + "F39", {"entities" : qUnion([Q0]), "oppositeDirection" : true, "depth" : 100 * mm});
        }
        {
            var Q0;
            Q0=makeQuery(id+"F39.opExtrude","CAP_FACE",FACE,{"disambiguationData":[OSD([sQuery(id+"F38.wireOp",EDGE,"E27.bottom"),sQuery(id+"F38.wireOp",EDGE,"E27.top"),sQuery(id+"F38.wireOp",EDGE,"E27.left"),sQuery(id+"F38.wireOp",EDGE,"E27.right")])],"isStart":true});
            var sketch = newSketch(context, id + "F40", { "sketchPlane" : qUnion([Q0])});
            skLineSegment(sketch, "E28.bottom", {"start": v(-246.14, 61.17) * mm, "end": v(-286.14, 61.17) * mm});
            skLineSegment(sketch, "E28.top", {"start": v(-246.14, 21.17) * mm, "end": v(-286.14, 21.17) * mm});
            skLineSegment(sketch, "E28.left", {"start": v(-246.14, 61.17) * mm, "end": v(-246.14, 21.17) * mm});
            skLineSegment(sketch, "E28.right", {"start": v(-286.14, 61.17) * mm, "end": v(-286.14, 21.17) * mm});
            skSolve(sketch);
        }
        {
            var Q0;
            Q0 = qSketchRegion(id + "F40", true);
            extrude(context, id + "F41", {"entities" : qUnion([Q0]), "oppositeDirection" : true, "depth" : 105 * mm});
        }
        {
            var Q0;
            Q0=makeQuery(id+"F41.opExtrude","CAP_FACE",FACE,{"disambiguationData":[OSD([sQuery(id+"F40.wireOp",EDGE,"E28.bottom"),sQuery(id+"F40.wireOp",EDGE,"E28.top"),sQuery(id+"F40.wireOp",EDGE,"E28.left"),sQuery(id+"F40.wireOp",EDGE,"E28.right")])],"isStart":true});
            var sketch = newSketch(context, id + "F42", { "sketchPlane" : qUnion([Q0])});
            skLineSegment(sketch, "E29.bottom", {"start": v(-286.14, 21.17) * mm, "end": v(-246.14, 21.17) * mm});
            skLineSegment(sketch, "E29.top", {"start": v(-286.14, -18.83) * mm, "end": v(-246.14, -18.83) * mm});
            skLineSegment(sketch, "E29.left", {"start": v(-286.14, 21.17) * mm, "end": v(-286.14, -18.83) * mm});
            skLineSegment(sketch, "E29.right", {"start": v(-246.14, 21.17) * mm, "end": v(-246.14, -18.83) * mm});
            skSolve(sketch);
        }
        {
            var Q0;
            Q0 = qSketchRegion(id + "F42", true);
            extrude(context, id + "F43", {"entities" : qUnion([Q0]), "oppositeDirection" : true, "depth" : 110 * mm});
        }
        {
            var Q0;
            Q0=makeQuery(id+"F43.opExtrude","CAP_FACE",FACE,{"disambiguationData":[OSD([sQuery(id+"F42.wireOp",EDGE,"E29.bottom"),sQuery(id+"F42.wireOp",EDGE,"E29.top"),sQuery(id+"F42.wireOp",EDGE,"E29.left"),sQuery(id+"F42.wireOp",EDGE,"E29.right")])],"isStart":true});
            var sketch = newSketch(context, id + "F44", { "sketchPlane" : qUnion([Q0])});
            skLineSegment(sketch, "E30.bottom", {"start": v(-246.14, -18.83) * mm, "end": v(-286.14, -18.83) * mm});
            skLineSegment(sketch, "E30.top", {"start": v(-246.14, -58.83) * mm, "end": v(-286.14, -58.83) * mm});
            skLineSegment(sketch, "E30.left", {"start": v(-246.14, -18.83) * mm, "end": v(-246.14, -58.83) * mm});
            skLineSegment(sketch, "E30.right", {"start": v(-286.14, -18.83) * mm, "end": v(-286.14, -58.83) * mm});
            skSolve(sketch);
        }
        {
            var Q0;
            Q0 = qSketchRegion(id + "F44", true);
            extrude(context, id + "F45", {"entities" : qUnion([Q0]), "oppositeDirection" : true, "depth" : 115 * mm});
        }
        {
            var Q0;
            Q0=makeQuery(id+"F45.opExtrude","CAP_FACE",FACE,{"disambiguationData":[OSD([sQuery(id+"F44.wireOp",EDGE,"E30.bottom"),sQuery(id+"F44.wireOp",EDGE,"E30.top"),sQuery(id+"F44.wireOp",EDGE,"E30.left"),sQuery(id+"F44.wireOp",EDGE,"E30.right")])],"isStart":true});
            var sketch = newSketch(context, id + "F46", { "sketchPlane" : qUnion([Q0])});
            skLineSegment(sketch, "E31.bottom", {"start": v(-246.14, -18.83) * mm, "end": v(-246.14, -18.83) * mm});
            skLineSegment(sketch, "E31.top", {"start": v(-246.14, -58.83) * mm, "end": v(-246.14, -58.83) * mm});
            skLineSegment(sketch, "E31.left", {"start": v(-246.14, -18.83) * mm, "end": v(-246.14, -58.83) * mm});
            skLineSegment(sketch, "E31.right", {"start": v(-246.14, -18.83) * mm, "end": v(-246.14, -58.83) * mm});
            skLineSegment(sketch, "E32.bottom", {"start": v(-246.14, -18.83) * mm, "end": v(-206.14, -18.83) * mm});
            skLineSegment(sketch, "E32.top", {"start": v(-246.14, -58.83) * mm, "end": v(-206.14, -58.83) * mm});
            skLineSegment(sketch, "E32.right", {"start": v(-206.14, -18.83) * mm, "end": v(-206.14, -58.83) * mm});
            skSolve(sketch);
        }
        {
            var Q0;
            Q0 = qSketchRegion(id + "F46", true);
            extrude(context, id + "F47", {"entities" : qUnion([Q0]), "oppositeDirection" : true, "depth" : 120 * mm});
        }
        {
            var Q0;
            Q0=makeQuery(id+"F47.opExtrude","CAP_FACE",FACE,{"disambiguationData":[OSD([sQuery(id+"F46.wireOp",EDGE,"E32.bottom"),sQuery(id+"F46.wireOp",EDGE,"E32.top"),sQuery(id+"F46.wireOp",EDGE,"E31.left"),sQuery(id+"F46.wireOp",EDGE,"E32.right")])],"isStart":true});
            var sketch = newSketch(context, id + "F48", { "sketchPlane" : qUnion([Q0])});
            skLineSegment(sketch, "E33.bottom", {"start": v(-206.14, -18.83) * mm, "end": v(-246.14, -18.83) * mm});
            skLineSegment(sketch, "E33.top", {"start": v(-206.14, 21.17) * mm, "end": v(-246.14, 21.17) * mm});
            skLineSegment(sketch, "E33.left", {"start": v(-206.14, -18.83) * mm, "end": v(-206.14, 21.17) * mm});
            skLineSegment(sketch, "E33.right", {"start": v(-246.14, -18.83) * mm, "end": v(-246.14, 21.17) * mm});
            skSolve(sketch);
        }
        {
            var Q0;
            Q0 = qSketchRegion(id + "F48", true);
            extrude(context, id + "F49", {"entities" : qUnion([Q0]), "oppositeDirection" : true, "depth" : 125 * mm});
        }
        {
            var Q0;
            Q0=makeQuery(id+"F1.opExtrude","CAP_FACE",FACE,{"disambiguationData":[OSD([sQuery(id+"F0.wireOp",EDGE,"E0.bottom"),sQuery(id+"F0.wireOp",EDGE,"E0.left"),sQuery(id+"F0.wireOp",EDGE,"E1"),sQuery(id+"F0.wireOp",EDGE,"E5")])],"isStart":false});
            var sketch = newSketch(context, id + "F50", { "sketchPlane" : qUnion([Q0])});
            skText(sketch, "E34", { "text": "1", "fontName": "OpenSans-Bold.ttf"});
            const initialGuessF50  = {"E34": [-0.1619, 0.0629, 1, 0, 0.03165]};
            skSetInitialGuess(sketch, initialGuessF50);
            skSolve(sketch);
        }
        {
            var Q0;
            Q0 = qSketchRegion(id + "F50", true);
            extrude(context, id + "F51", {"entities" : qUnion([Q0]), "operationType" : NewBodyOperationType.REMOVE, "oppositeDirection" : true, "depth" : 25.4 * mm});
        }
        {
            var Q0;
            Q0=makeQuery(id+"F3.opExtrude","CAP_FACE",FACE,{"disambiguationData":[OSD([sQuery(id+"F2.wireOp",EDGE,"E9.bottom"),sQuery(id+"F2.wireOp",EDGE,"E9.top"),sQuery(id+"F2.wireOp",EDGE,"E9.left"),sQuery(id+"F2.wireOp",EDGE,"E9.right")])],"isStart":false});
            var sketch = newSketch(context, id + "F52", { "sketchPlane" : qUnion([Q0])});
            skText(sketch, "E35", { "text": "2", "fontName": "OpenSans-Bold.ttf"});
            const initialGuessF52  = {"E35": [-0.15934, 0.02303, 1, 0, 0.03082]};
            skSetInitialGuess(sketch, initialGuessF52);
            skSolve(sketch);
        }
        {
            var Q0;
            Q0 = qSketchRegion(id + "F52", true);
            extrude(context, id + "F53", {"entities" : qUnion([Q0]), "operationType" : NewBodyOperationType.REMOVE, "oppositeDirection" : true, "depth" : 5 * mm});
        }
        {
            var Q0;
            Q0=makeQuery(id+"F5.opExtrude","CAP_FACE",FACE,{"disambiguationData":[OSD([sQuery(id+"F4.wireOp",EDGE,"E10.bottom"),sQuery(id+"F4.wireOp",EDGE,"E10.top"),sQuery(id+"F4.wireOp",EDGE,"E10.left"),sQuery(id+"F4.wireOp",EDGE,"E10.right")])],"isStart":false});
            var sketch = newSketch(context, id + "F54", { "sketchPlane" : qUnion([Q0])});
            skText(sketch, "E36", { "text": "3", "fontName": "OpenSans-Bold.ttf"});
            const initialGuessF54  = {"E36": [-0.15844, -0.01667, 1, 0, 0.03003]};
            skSetInitialGuess(sketch, initialGuessF54);
            skSolve(sketch);
        }
        {
            var Q0;
            Q0 = qSketchRegion(id + "F54", true);
            extrude(context, id + "F55", {"entities" : qUnion([Q0]), "operationType" : NewBodyOperationType.REMOVE, "oppositeDirection" : true, "depth" : 5 * mm});
        }
        {
            var Q0;
            Q0=makeQuery(id+"F7.opExtrude","CAP_FACE",FACE,{"disambiguationData":[OSD([sQuery(id+"F6.wireOp",EDGE,"E11.bottom"),sQuery(id+"F6.wireOp",EDGE,"E11.top"),sQuery(id+"F6.wireOp",EDGE,"E11.left"),sQuery(id+"F6.wireOp",EDGE,"E11.right")])],"isStart":false});
            var sketch = newSketch(context, id + "F56", { "sketchPlane" : qUnion([Q0])});
            skText(sketch, "E37", { "text": "4", "fontName": "OpenSans-Bold.ttf"});
            const initialGuessF56  = {"E37": [-0.15996, -0.05662, 1, 0, 0.03063]};
            skSetInitialGuess(sketch, initialGuessF56);
            skSolve(sketch);
        }
        {
            var Q0;
            Q0 = qSketchRegion(id + "F56", true);
            extrude(context, id + "F57", {"entities" : qUnion([Q0]), "operationType" : NewBodyOperationType.REMOVE, "oppositeDirection" : true, "depth" : 5 * mm});
        }
        {
            var Q0;
            Q0=makeQuery(id+"F9.opExtrude","CAP_FACE",FACE,{"disambiguationData":[OSD([sQuery(id+"F8.wireOp",EDGE,"E12.bottom"),sQuery(id+"F8.wireOp",EDGE,"E12.top"),sQuery(id+"F8.wireOp",EDGE,"E12.left"),sQuery(id+"F8.wireOp",EDGE,"E12.right")])],"isStart":false});
            var sketch = newSketch(context, id + "F58", { "sketchPlane" : qUnion([Q0])});
            skText(sketch, "E38", { "text": "5", "fontName": "OpenSans-Bold.ttf"});
            const initialGuessF58  = {"E38": [-0.15867, -0.09692, 1, 0, 0.0303]};
            skSetInitialGuess(sketch, initialGuessF58);
            skSolve(sketch);
        }
        {
            var Q0;
            Q0 = qSketchRegion(id + "F58", true);
            extrude(context, id + "F59", {"entities" : qUnion([Q0]), "operationType" : NewBodyOperationType.REMOVE, "oppositeDirection" : true, "depth" : 5 * mm});
        }
        {
            var Q0;
            Q0=makeQuery(id+"F11.opExtrude","CAP_FACE",FACE,{"disambiguationData":[OSD([sQuery(id+"F10.wireOp",EDGE,"E13.bottom"),sQuery(id+"F10.wireOp",EDGE,"E13.top"),sQuery(id+"F10.wireOp",EDGE,"E13.left"),sQuery(id+"F10.wireOp",EDGE,"E13.right")])],"isStart":false});
            var sketch = newSketch(context, id + "F60", { "sketchPlane" : qUnion([Q0])});
            skText(sketch, "E39", { "text": "6", "fontName": "OpenSans-Bold.ttf"});
            const initialGuessF60  = {"E39": [-0.19962, -0.09756, 1, 0, 0.03256]};
            skSetInitialGuess(sketch, initialGuessF60);
            skSolve(sketch);
        }
        {
            var Q0;
            Q0 = qSketchRegion(id + "F60", true);
            extrude(context, id + "F61", {"entities" : qUnion([Q0]), "operationType" : NewBodyOperationType.REMOVE, "oppositeDirection" : true, "depth" : 5 * mm});
        }
        {
            var Q0;
            Q0=makeQuery(id+"F13.opExtrude","CAP_FACE",FACE,{"disambiguationData":[OSD([sQuery(id+"F12.wireOp",EDGE,"E14.bottom"),sQuery(id+"F12.wireOp",EDGE,"E14.top"),sQuery(id+"F12.wireOp",EDGE,"E14.left"),sQuery(id+"F12.wireOp",EDGE,"E14.right")])],"isStart":false});
            var sketch = newSketch(context, id + "F62", { "sketchPlane" : qUnion([Q0])});
            skText(sketch, "E40", { "text": "7", "fontName": "OpenSans-Bold.ttf"});
            const initialGuessF62  = {"E40": [-0.239, -0.09686, 1, 0, 0.03108]};
            skSetInitialGuess(sketch, initialGuessF62);
            skSolve(sketch);
        }
        {
            var Q0;
            Q0 = qSketchRegion(id + "F62", true);
            extrude(context, id + "F63", {"entities" : qUnion([Q0]), "operationType" : NewBodyOperationType.REMOVE, "oppositeDirection" : true, "depth" : 5 * mm});
        }
        {
            var Q0;
            Q0=makeQuery(id+"F15.opExtrude","CAP_FACE",FACE,{"disambiguationData":[OSD([sQuery(id+"F14.wireOp",EDGE,"E15.bottom"),sQuery(id+"F14.wireOp",EDGE,"E15.top"),sQuery(id+"F14.wireOp",EDGE,"E15.left"),sQuery(id+"F14.wireOp",EDGE,"E15.right")])],"isStart":false});
            var sketch = newSketch(context, id + "F64", { "sketchPlane" : qUnion([Q0])});
            skText(sketch, "E41", { "text": "8", "fontName": "OpenSans-Bold.ttf"});
            const initialGuessF64  = {"E41": [-0.28033, -0.0972, 1, 0, 0.0321]};
            skSetInitialGuess(sketch, initialGuessF64);
            skSolve(sketch);
        }
        {
            var Q0;
            Q0 = qSketchRegion(id + "F64", true);
            extrude(context, id + "F65", {"entities" : qUnion([Q0]), "operationType" : NewBodyOperationType.REMOVE, "oppositeDirection" : true, "depth" : 5 * mm});
        }
        {
            var Q0;
            Q0=makeQuery(id+"F17.opExtrude","CAP_FACE",FACE,{"disambiguationData":[OSD([sQuery(id+"F16.wireOp",EDGE,"E16.bottom"),sQuery(id+"F16.wireOp",EDGE,"E16.top"),sQuery(id+"F16.wireOp",EDGE,"E16.left"),sQuery(id+"F16.wireOp",EDGE,"E16.right")])],"isStart":false});
            var sketch = newSketch(context, id + "F66", { "sketchPlane" : qUnion([Q0])});
            skText(sketch, "E42", { "text": "9", "fontName": "OpenSans-Bold.ttf"});
            const initialGuessF66  = {"E42": [-0.31961, -0.09702, 1, 0, 0.03174]};
            skSetInitialGuess(sketch, initialGuessF66);
            skSolve(sketch);
        }
        {
            var Q0;
            Q0 = qSketchRegion(id + "F66", true);
            extrude(context, id + "F67", {"entities" : qUnion([Q0]), "operationType" : NewBodyOperationType.REMOVE, "oppositeDirection" : true, "depth" : 5 * mm});
        }
        {
            var Q0;
            Q0=makeQuery(id+"F19.opExtrude","CAP_FACE",FACE,{"disambiguationData":[OSD([sQuery(id+"F18.wireOp",EDGE,"E17.bottom"),sQuery(id+"F18.wireOp",EDGE,"E17.top"),sQuery(id+"F18.wireOp",EDGE,"E17.left"),sQuery(id+"F18.wireOp",EDGE,"E17.right")])],"isStart":false});
            var sketch = newSketch(context, id + "F68", { "sketchPlane" : qUnion([Q0])});
            skText(sketch, "E43", { "text": "10", "fontName": "OpenSans-Bold.ttf"});
            const initialGuessF68  = {"E43": [-0.32425, -0.0524, 1, 0, 0.02152]};
            skSetInitialGuess(sketch, initialGuessF68);
            skSolve(sketch);
        }
        {
            var Q0;
            Q0 = qSketchRegion(id + "F68", true);
            extrude(context, id + "F69", {"entities" : qUnion([Q0]), "operationType" : NewBodyOperationType.REMOVE, "oppositeDirection" : true, "depth" : 5 * mm});
        }
        {
            var Q0;
            Q0=makeQuery(id+"F21.opExtrude","CAP_FACE",FACE,{"disambiguationData":[OSD([sQuery(id+"F20.wireOp",EDGE,"E18.bottom"),sQuery(id+"F20.wireOp",EDGE,"E18.top"),sQuery(id+"F20.wireOp",EDGE,"E18.left"),sQuery(id+"F20.wireOp",EDGE,"E18.right")])],"isStart":false});
            var sketch = newSketch(context, id + "F70", { "sketchPlane" : qUnion([Q0])});
            skText(sketch, "E44", { "text": "11", "fontName": "OpenSans-Bold.ttf"});
            const initialGuessF70  = {"E44": [-0.32384, -0.0132, 1, 0, 0.02403]};
            skSetInitialGuess(sketch, initialGuessF70);
            skSolve(sketch);
        }
        {
            var Q0;
            Q0 = qSketchRegion(id + "F70", true);
            extrude(context, id + "F71", {"entities" : qUnion([Q0]), "operationType" : NewBodyOperationType.REMOVE, "oppositeDirection" : true, "depth" : 5 * mm});
        }
        {
            var Q0;
            Q0=makeQuery(id+"F23.opExtrude","CAP_FACE",FACE,{"disambiguationData":[OSD([sQuery(id+"F22.wireOp",EDGE,"E19.bottom"),sQuery(id+"F22.wireOp",EDGE,"E19.top"),sQuery(id+"F22.wireOp",EDGE,"E19.left"),sQuery(id+"F22.wireOp",EDGE,"E19.right")])],"isStart":false});
            var sketch = newSketch(context, id + "F72", { "sketchPlane" : qUnion([Q0])});
            skText(sketch, "E45", { "text": "12", "fontName": "OpenSans-Bold.ttf"});
            const initialGuessF72  = {"E45": [-0.32428, 0.02694, 1, 0, 0.02145]};
            skSetInitialGuess(sketch, initialGuessF72);
            skSolve(sketch);
        }
        {
            var Q0;
            Q0 = qSketchRegion(id + "F72", true);
            extrude(context, id + "F73", {"entities" : qUnion([Q0]), "operationType" : NewBodyOperationType.REMOVE, "oppositeDirection" : true, "depth" : 5 * mm});
        }
        {
            var Q0;
            Q0=makeQuery(id+"F25.opExtrude","CAP_FACE",FACE,{"disambiguationData":[OSD([sQuery(id+"F24.wireOp",EDGE,"E20.bottom"),sQuery(id+"F24.wireOp",EDGE,"E20.top"),sQuery(id+"F24.wireOp",EDGE,"E20.left"),sQuery(id+"F24.wireOp",EDGE,"E20.right")])],"isStart":false});
            var sketch = newSketch(context, id + "F74", { "sketchPlane" : qUnion([Q0])});
            skText(sketch, "E46", { "text": "13", "fontName": "OpenSans-Bold.ttf"});
            const initialGuessF74  = {"E46": [-0.32357, 0.06713, 1, 0, 0.02158]};
            skSetInitialGuess(sketch, initialGuessF74);
            skSolve(sketch);
        }
        {
            var Q0;
            Q0 = qSketchRegion(id + "F74", true);
            extrude(context, id + "F75", {"entities" : qUnion([Q0]), "operationType" : NewBodyOperationType.REMOVE, "oppositeDirection" : true, "depth" : 5 * mm});
        }
        {
            var Q0;
            Q0=makeQuery(id+"F27.opExtrude","CAP_FACE",FACE,{"disambiguationData":[OSD([sQuery(id+"F26.wireOp",EDGE,"E21.bottom"),sQuery(id+"F26.wireOp",EDGE,"E21.top"),sQuery(id+"F26.wireOp",EDGE,"E21.left"),sQuery(id+"F26.wireOp",EDGE,"E21.right")])],"isStart":false});
            var sketch = newSketch(context, id + "F76", { "sketchPlane" : qUnion([Q0])});
            skText(sketch, "E47", { "text": "14", "fontName": "OpenSans-Bold.ttf"});
            const initialGuessF76  = {"E47": [-0.28389, 0.06758, 1, 0, 0.02116]};
            skSetInitialGuess(sketch, initialGuessF76);
            skSolve(sketch);
        }
        {
            var Q0;
            Q0 = qSketchRegion(id + "F76", true);
            extrude(context, id + "F77", {"entities" : qUnion([Q0]), "operationType" : NewBodyOperationType.REMOVE, "oppositeDirection" : true, "depth" : 5 * mm});
        }
        {
            var Q0;
            Q0=makeQuery(id+"F29.opExtrude","CAP_FACE",FACE,{"disambiguationData":[OSD([sQuery(id+"F28.wireOp",EDGE,"E22.bottom"),sQuery(id+"F28.wireOp",EDGE,"E22.top"),sQuery(id+"F28.wireOp",EDGE,"E22.left"),sQuery(id+"F28.wireOp",EDGE,"E22.right")])],"isStart":false});
            var sketch = newSketch(context, id + "F78", { "sketchPlane" : qUnion([Q0])});
            skText(sketch, "E48", { "text": "15", "fontName": "OpenSans-Bold.ttf"});
            const initialGuessF78  = {"E48": [-0.24357, 0.067, 1, 0, 0.0217]};
            skSetInitialGuess(sketch, initialGuessF78);
            skSolve(sketch);
        }
        {
            var Q0;
            Q0 = qSketchRegion(id + "F78", true);
            extrude(context, id + "F79", {"entities" : qUnion([Q0]), "operationType" : NewBodyOperationType.REMOVE, "oppositeDirection" : true, "depth" : 5 * mm});
        }
        {
            var Q0;
            Q0=makeQuery(id+"F31.opExtrude","CAP_FACE",FACE,{"disambiguationData":[OSD([sQuery(id+"F30.wireOp",EDGE,"E23.bottom"),sQuery(id+"F30.wireOp",EDGE,"E23.top"),sQuery(id+"F30.wireOp",EDGE,"E23.left"),sQuery(id+"F30.wireOp",EDGE,"E23.right")])],"isStart":false});
            var sketch = newSketch(context, id + "F80", { "sketchPlane" : qUnion([Q0])});
            skText(sketch, "E49", { "text": "16", "fontName": "OpenSans-Bold.ttf"});
            const initialGuessF80  = {"E49": [-0.2039, 0.06733, 1, 0, 0.02145]};
            skSetInitialGuess(sketch, initialGuessF80);
            skSolve(sketch);
        }
        {
            var Q0;
            Q0 = qSketchRegion(id + "F80", true);
            extrude(context, id + "F81", {"entities" : qUnion([Q0]), "operationType" : NewBodyOperationType.REMOVE, "oppositeDirection" : true, "depth" : 5 * mm});
        }
        {
            var Q0;
            Q0=makeQuery(id+"F33.opExtrude","CAP_FACE",FACE,{"disambiguationData":[OSD([sQuery(id+"F32.wireOp",EDGE,"E24.bottom"),sQuery(id+"F32.wireOp",EDGE,"E24.top"),sQuery(id+"F32.wireOp",EDGE,"E24.left"),sQuery(id+"F32.wireOp",EDGE,"E24.right")])],"isStart":false});
            var sketch = newSketch(context, id + "F82", { "sketchPlane" : qUnion([Q0])});
            skText(sketch, "E50", { "text": "17", "fontName": "OpenSans-Bold.ttf"});
            const initialGuessF82  = {"E50": [-0.20351, 0.0272, 1, 0, 0.02145]};
            skSetInitialGuess(sketch, initialGuessF82);
            skSolve(sketch);
        }
        {
            var Q0;
            Q0 = qSketchRegion(id + "F82", true);
            extrude(context, id + "F83", {"entities" : qUnion([Q0]), "operationType" : NewBodyOperationType.REMOVE, "oppositeDirection" : true, "depth" : 5 * mm});
        }
        {
            var Q0;
            Q0=makeQuery(id+"F35.opExtrude","CAP_FACE",FACE,{"disambiguationData":[OSD([sQuery(id+"F34.wireOp",EDGE,"E25.bottom"),sQuery(id+"F34.wireOp",EDGE,"E25.top"),sQuery(id+"F34.wireOp",EDGE,"E25.left"),sQuery(id+"F34.wireOp",EDGE,"E25.right")])],"isStart":false});
            var sketch = newSketch(context, id + "F84", { "sketchPlane" : qUnion([Q0])});
            skText(sketch, "E51", { "text": "18", "fontName": "OpenSans-Bold.ttf"});
            const initialGuessF84  = {"E51": [-0.2035, -0.01147, 1, 0, 0.0215]};
            skSetInitialGuess(sketch, initialGuessF84);
            skSolve(sketch);
        }
        {
            var Q0;
            Q0 = qSketchRegion(id + "F84", true);
            extrude(context, id + "F85", {"entities" : qUnion([Q0]), "operationType" : NewBodyOperationType.REMOVE, "oppositeDirection" : true, "depth" : 5 * mm});
        }
        {
            var Q0;
            Q0=makeQuery(id+"F37.opExtrude","CAP_FACE",FACE,{"disambiguationData":[OSD([sQuery(id+"F36.wireOp",EDGE,"E26.bottom"),sQuery(id+"F36.wireOp",EDGE,"E26.top"),sQuery(id+"F36.wireOp",EDGE,"E26.left"),sQuery(id+"F36.wireOp",EDGE,"E26.right")])],"isStart":false});
            var sketch = newSketch(context, id + "F86", { "sketchPlane" : qUnion([Q0])});
            skText(sketch, "E52", { "text": "19", "fontName": "OpenSans-Bold.ttf"});
            const initialGuessF86  = {"E52": [-0.20344, -0.05266, 1, 0, 0.0215]};
            skSetInitialGuess(sketch, initialGuessF86);
            skSolve(sketch);
        }
        {
            var Q0;
            Q0 = qSketchRegion(id + "F86", true);
            extrude(context, id + "F87", {"entities" : qUnion([Q0]), "operationType" : NewBodyOperationType.REMOVE, "oppositeDirection" : true, "depth" : 5 * mm});
        }
        {
            var Q0;
            Q0=makeQuery(id+"F39.opExtrude","CAP_FACE",FACE,{"disambiguationData":[OSD([sQuery(id+"F38.wireOp",EDGE,"E27.bottom"),sQuery(id+"F38.wireOp",EDGE,"E27.top"),sQuery(id+"F38.wireOp",EDGE,"E27.left"),sQuery(id+"F38.wireOp",EDGE,"E27.right")])],"isStart":false});
            var sketch = newSketch(context, id + "F88", { "sketchPlane" : qUnion([Q0])});
            skText(sketch, "E53", { "text": "20", "fontName": "OpenSans-Bold.ttf"});
            const initialGuessF88  = {"E53": [-0.24382, -0.05173, 1, 0, 0.02152]};
            skSetInitialGuess(sketch, initialGuessF88);
            skSolve(sketch);
        }
        {
            var Q0;
            Q0 = qSketchRegion(id + "F88", true);
            extrude(context, id + "F89", {"entities" : qUnion([Q0]), "operationType" : NewBodyOperationType.REMOVE, "oppositeDirection" : true, "depth" : 5 * mm});
        }
        {
            var Q0;
            Q0=makeQuery(id+"F41.opExtrude","CAP_FACE",FACE,{"disambiguationData":[OSD([sQuery(id+"F40.wireOp",EDGE,"E28.bottom"),sQuery(id+"F40.wireOp",EDGE,"E28.top"),sQuery(id+"F40.wireOp",EDGE,"E28.left"),sQuery(id+"F40.wireOp",EDGE,"E28.right")])],"isStart":false});
            var sketch = newSketch(context, id + "F90", { "sketchPlane" : qUnion([Q0])});
            skText(sketch, "E54", { "text": "21", "fontName": "OpenSans-Bold.ttf"});
            const initialGuessF90  = {"E54": [-0.28332, -0.05354, 1, 0, 0.02403]};
            skSetInitialGuess(sketch, initialGuessF90);
            skSolve(sketch);
        }
        {
            var Q0;
            Q0 = qSketchRegion(id + "F90", true);
            extrude(context, id + "F91", {"entities" : qUnion([Q0]), "operationType" : NewBodyOperationType.REMOVE, "oppositeDirection" : true, "depth" : 5 * mm});
        }
        {
            var Q0;
            Q0=makeQuery(id+"F43.opExtrude","CAP_FACE",FACE,{"disambiguationData":[OSD([sQuery(id+"F42.wireOp",EDGE,"E29.bottom"),sQuery(id+"F42.wireOp",EDGE,"E29.top"),sQuery(id+"F42.wireOp",EDGE,"E29.left"),sQuery(id+"F42.wireOp",EDGE,"E29.right")])],"isStart":false});
            var sketch = newSketch(context, id + "F92", { "sketchPlane" : qUnion([Q0])});
            skText(sketch, "E55", { "text": "22", "fontName": "OpenSans-Bold.ttf"});
            const initialGuessF92  = {"E55": [-0.28366, -0.01173, 1, 0, 0.02145]};
            skSetInitialGuess(sketch, initialGuessF92);
            skSolve(sketch);
        }
        {
            var Q0;
            Q0 = qSketchRegion(id + "F92", true);
            extrude(context, id + "F93", {"entities" : qUnion([Q0]), "operationType" : NewBodyOperationType.REMOVE, "oppositeDirection" : true, "depth" : 5 * mm});
        }
        {
            var Q0;
            Q0=makeQuery(id+"F45.opExtrude","CAP_FACE",FACE,{"disambiguationData":[OSD([sQuery(id+"F44.wireOp",EDGE,"E30.bottom"),sQuery(id+"F44.wireOp",EDGE,"E30.top"),sQuery(id+"F44.wireOp",EDGE,"E30.left"),sQuery(id+"F44.wireOp",EDGE,"E30.right")])],"isStart":false});
            var sketch = newSketch(context, id + "F94", { "sketchPlane" : qUnion([Q0])});
            skText(sketch, "E56", { "text": "23", "fontName": "OpenSans-Bold.ttf"});
            const initialGuessF94  = {"E56": [-0.28448, 0.0271, 1, 0, 0.02158]};
            skSetInitialGuess(sketch, initialGuessF94);
            skSolve(sketch);
        }
        {
            var Q0;
            Q0 = qSketchRegion(id + "F94", true);
            extrude(context, id + "F95", {"entities" : qUnion([Q0]), "operationType" : NewBodyOperationType.REMOVE, "oppositeDirection" : true, "depth" : 5 * mm});
        }
        {
            var Q0;
            Q0=makeQuery(id+"F47.opExtrude","CAP_FACE",FACE,{"disambiguationData":[OSD([sQuery(id+"F46.wireOp",EDGE,"E32.bottom"),sQuery(id+"F46.wireOp",EDGE,"E32.top"),sQuery(id+"F46.wireOp",EDGE,"E31.left"),sQuery(id+"F46.wireOp",EDGE,"E32.right")])],"isStart":false});
            var sketch = newSketch(context, id + "F96", { "sketchPlane" : qUnion([Q0])});
            skText(sketch, "E57", { "text": "24", "fontName": "OpenSans-Bold.ttf"});
            const initialGuessF96  = {"E57": [-0.24374, 0.0266, 1, 0, 0.02116]};
            skSetInitialGuess(sketch, initialGuessF96);
            skSolve(sketch);
        }
        {
            var Q0;
            Q0 = qSketchRegion(id + "F96", true);
            extrude(context, id + "F97", {"entities" : qUnion([Q0]), "operationType" : NewBodyOperationType.REMOVE, "oppositeDirection" : true, "depth" : 5 * mm});
        }
        {
            var Q0;
            Q0=makeQuery(id+"F49.opExtrude","CAP_FACE",FACE,{"disambiguationData":[OSD([sQuery(id+"F48.wireOp",EDGE,"E33.bottom"),sQuery(id+"F48.wireOp",EDGE,"E33.top"),sQuery(id+"F48.wireOp",EDGE,"E33.left"),sQuery(id+"F48.wireOp",EDGE,"E33.right")])],"isStart":false});
            var sketch = newSketch(context, id + "F98", { "sketchPlane" : qUnion([Q0])});
            skText(sketch, "E58", { "text": "25", "fontName": "OpenSans-Bold.ttf"});
            const initialGuessF98  = {"E58": [-0.24401, -0.01336, 1, 0, 0.0217]};
            skSetInitialGuess(sketch, initialGuessF98);
            skSolve(sketch);
        }
        {
            var Q0;
            Q0 = qSketchRegion(id + "F98", true);
            extrude(context, id + "F99", {"entities" : qUnion([Q0]), "operationType" : NewBodyOperationType.REMOVE, "oppositeDirection" : true, "depth" : 5 * mm});
        }
        {
            var Q0;
            Q0=makeQuery(id+"F49.opExtrude","CAP_FACE",FACE,{"disambiguationData":[OSD([sQuery(id+"F48.wireOp",EDGE,"E33.bottom"),sQuery(id+"F48.wireOp",EDGE,"E33.top"),sQuery(id+"F48.wireOp",EDGE,"E33.left"),sQuery(id+"F48.wireOp",EDGE,"E33.right")])],"isStart":true});
            var sketch = newSketch(context, id + "F100", { "sketchPlane" : qUnion([Q0])});
            skPoint(sketch, "E59.centerSnap0", {"position": v(-226.14, -18.83) * mm});
            skPoint(sketch, "E59.centerSnap1", {"position": v(-206.14, 1.17) * mm});
            skLineSegment(sketch, "E60", {"start": v(-225.39, 57.27) * mm, "end": v(-225.39, -54.93) * mm});
            skArc(sketch, "E61", {"start": v(-225.39, 57.27) * mm, "mid": v(-282.25, 1.17) * mm, "end": v(-225.39, -54.93) * mm});
            skSolve(sketch);
        }
        {
            var Q0;
            {var subQ0=sQuery(id+"F100.wireOp",EDGE,"E61");Q0=makeQuery(id+"F100.imprint","IMPRINT",FACE,{"disambiguationData":[TD([[makeQuery(id+"F100.imprint","IMPRINT",EDGE,{"derivedFrom":subQ0}),1.0]])]});}
            var Q1;
            Q1=sQuery(id+"F100.wireOp",EDGE,"E60");
            revolve(context, id + "F101", {"operationType" : NewBodyOperationType.REMOVE, "entities" : qUnion([Q0]), "axis" : qUnion([Q1]), "revolveType" : RevolveType.ONE_DIRECTION, "angle" : 180 * degree});
        }
        {
            var Q0;
            Q0=makeQuery(id+"F49.opExtrude","CAP_FACE",FACE,{"disambiguationData":[OSD([sQuery(id+"F48.wireOp",EDGE,"E33.bottom"),sQuery(id+"F48.wireOp",EDGE,"E33.top"),sQuery(id+"F48.wireOp",EDGE,"E33.left"),sQuery(id+"F48.wireOp",EDGE,"E33.right")])],"isStart":true});
            var sketch = newSketch(context, id + "F102", { "sketchPlane" : qUnion([Q0])});
            skLineSegment(sketch, "E62.bottom", {"start": v(-126.14, -98.83) * mm, "end": v(-326.14, -98.83) * mm});
            skLineSegment(sketch, "E62.top", {"start": v(-126.14, 101.17) * mm, "end": v(-326.14, 101.17) * mm});
            skLineSegment(sketch, "E62.left", {"start": v(-126.14, -98.83) * mm, "end": v(-126.14, 101.17) * mm});
            skLineSegment(sketch, "E62.right", {"start": v(-326.14, -98.83) * mm, "end": v(-326.14, 101.17) * mm});
            skPoint(sketch, "E62.middle", {"position": v(-226.14, 1.17) * mm});
            skPoint(sketch, "E62.middle.positionSnap0", {"position": v(-246.14, 1.17) * mm});
            skPoint(sketch, "E62.middle.positionSnap1", {"position": v(-226.14, -18.83) * mm});
            skPoint(sketch, "E62.centerSnap0", {"position": v(-246.14, 1.17) * mm});
            skPoint(sketch, "E62.centerSnap1", {"position": v(-226.14, -18.83) * mm});
            skSolve(sketch);
        }
        {
            var Q0;
            Q0 = qSketchRegion(id + "F102", true);
            extrude(context, id + "F103", {"entities" : qUnion([Q0]), "depth" : 2.54 * mm});
        }
    });
